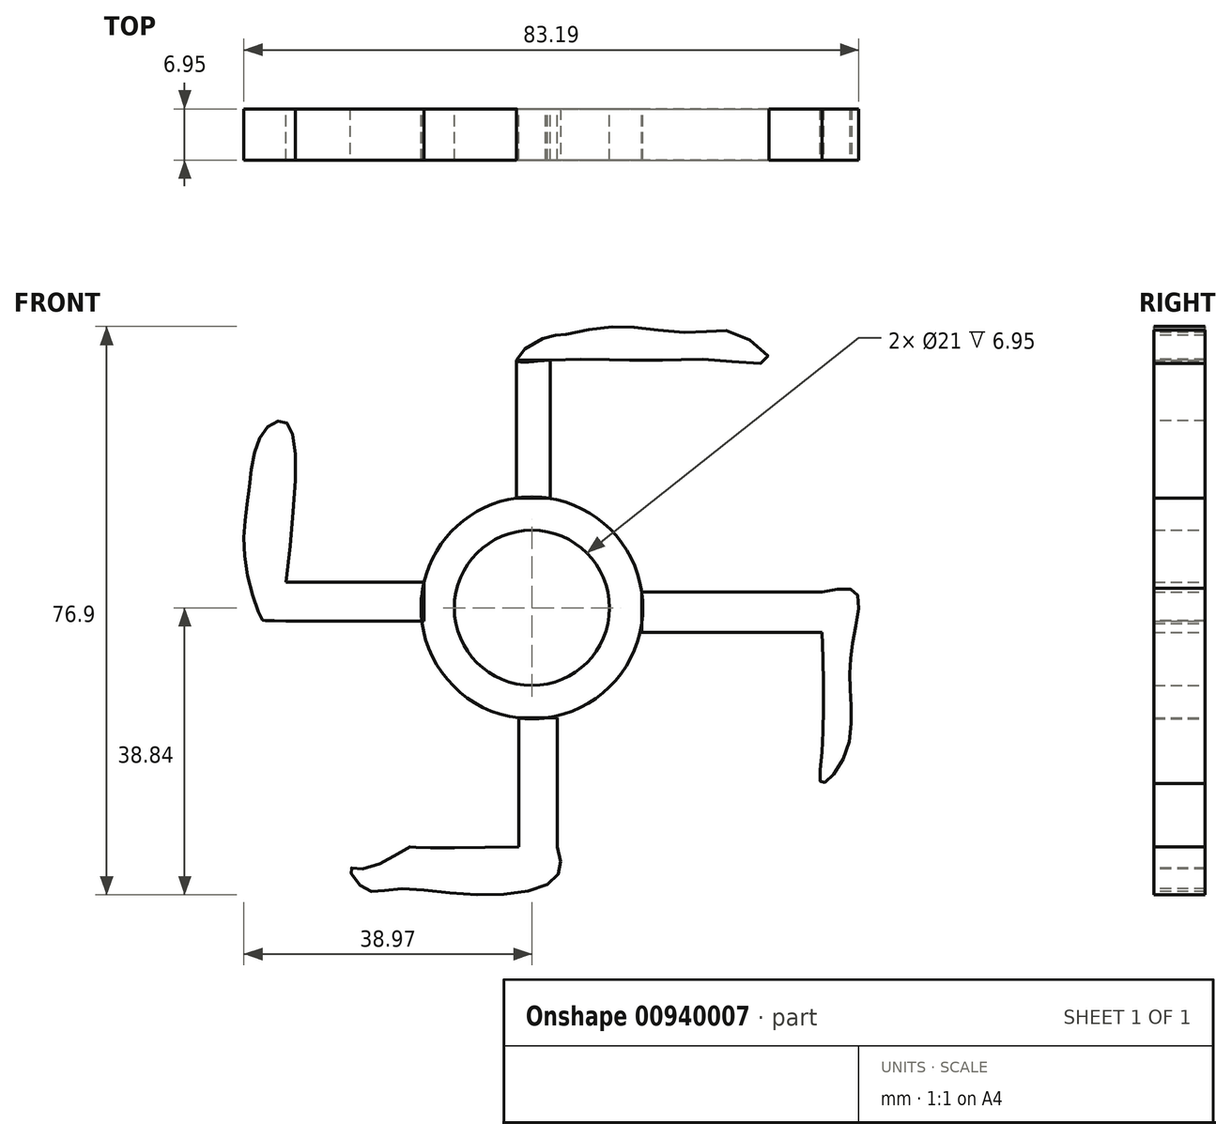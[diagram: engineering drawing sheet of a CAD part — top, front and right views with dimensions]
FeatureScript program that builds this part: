
annotation { "Feature Type Name" : "Feature", "Feature Type Description" : "" }
export const myFeature = defineFeature(function(context is Context, id is Id, definition is map)
    precondition{}
    {
        {
            var Q0;
            Q0=qCreatedBy(makeId("Front.planeOp"),FACE);
            var sketch = newSketch(context, id + "F0", { "sketchPlane" : qUnion([Q0])});
            skCircle(sketch, "E0", {"center": v(0, 0) * mm, "radius": 15 * mm});
            skCircle(sketch, "E1", {"center": v(0, 0) * mm, "radius": 10.5 * mm});
            skLineSegment(sketch, "E2.bottom", {"start": v(-2.08, 14.86) * mm, "end": v(2.45, 14.86) * mm});
            skLineSegment(sketch, "E2.top", {"start": v(-2.08, 33.54) * mm, "end": v(2.45, 33.54) * mm});
            skLineSegment(sketch, "E2.left", {"start": v(-2.08, 14.86) * mm, "end": v(-2.08, 33.54) * mm});
            skLineSegment(sketch, "E2.right", {"start": v(2.45, 14.86) * mm, "end": v(2.45, 33.54) * mm});
            skFitSpline(sketch, "E3", {"points": [v(-2.08, 33.54) * mm, v(0, 35.7) * mm, v(3.04, 36.87) * mm, v(3.63, 36.87) * mm, v(8.92, 37.85) * mm, v(14.8, 37.85) * mm, v(22.46, 37.27) * mm, v(27.36, 37.27) * mm, v(32.07, 33.54) * mm, v(24.81, 33.54) * mm, v(18.93, 33.54) * mm, v(15, 33.54) * mm, v(12.06, 33.54) * mm, v(2.45, 33.54) * mm, v(-2.08, 33.54) * mm]});
            skLineSegment(sketch, "E4.bottom", {"start": v(14.85, 2.11) * mm, "end": v(39.23, 2.11) * mm});
            skLineSegment(sketch, "E4.top", {"start": v(14.85, -3.33) * mm, "end": v(39.23, -3.33) * mm});
            skLineSegment(sketch, "E4.left", {"start": v(14.85, 2.11) * mm, "end": v(14.85, -3.33) * mm});
            skLineSegment(sketch, "E4.right", {"start": v(39.23, 2.11) * mm, "end": v(39.23, -3.33) * mm});
            skLineSegment(sketch, "E5.bottom", {"start": v(-1.8, -14.9) * mm, "end": v(3.43, -14.9) * mm});
            skLineSegment(sketch, "E5.top", {"start": v(-1.8, -32.36) * mm, "end": v(3.43, -32.36) * mm});
            skLineSegment(sketch, "E5.left", {"start": v(-1.8, -14.9) * mm, "end": v(-1.8, -32.36) * mm});
            skLineSegment(sketch, "E5.right", {"start": v(3.43, -14.9) * mm, "end": v(3.43, -32.36) * mm});
            skLineSegment(sketch, "E6.bottom", {"start": v(-14.6, 3.46) * mm, "end": v(-33.25, 3.46) * mm});
            skLineSegment(sketch, "E6.top", {"start": v(-14.6, -1.77) * mm, "end": v(-33.25, -1.77) * mm});
            skLineSegment(sketch, "E6.left", {"start": v(-14.6, 3.46) * mm, "end": v(-14.6, -1.77) * mm});
            skLineSegment(sketch, "E6.right", {"start": v(-33.25, 3.46) * mm, "end": v(-33.25, -1.77) * mm});
            skFitSpline(sketch, "E7", {"points": [v(3.43, -32.36) * mm, v(3.43, -36.29) * mm, v(-5.59, -38.84) * mm, v(-18.73, -38.05) * mm, v(-22.65, -38.05) * mm, v(-24.62, -35.3) * mm, v(-22.65, -35.3) * mm, v(-16.57, -32.36) * mm, v(-15.79, -32.36) * mm, v(-1.8, -32.36) * mm], "startDerivative": vector(12.64, -46.06) * mm, "endDerivative": vector(106.45, 1.35) * mm});
            skFitSpline(sketch, "E8", {"points": [v(-33.25, -1.77) * mm, v(-36.19, -1.77) * mm, v(-36.38, -1.77) * mm, v(-38.74, 5.88) * mm, v(-38.35, 15.5) * mm, v(-36.38, 23.73) * mm, v(-33.25, 25.1) * mm, v(-33.25, 3.46) * mm], "startDerivative": vector(-39.27, 1.4) * mm, "endDerivative": vector(-12.27, -113.4) * mm});
            skFitSpline(sketch, "E9", {"points": [v(39.23, 2.11) * mm, v(43.84, 2.11) * mm, v(43.44, -4.32) * mm, v(43.05, -10.98) * mm, v(42.46, -19.61) * mm, v(39.23, -23.73) * mm, v(39.23, -19.42) * mm, v(39.23, -3.33) * mm], "startDerivative": vector(50.34, 11.69) * mm, "endDerivative": vector(-2.74, 81.14) * mm});
            skSolve(sketch);
        }
        {
            var Q0;
            Q0=makeQuery(id+"F0.imprint","IMPRINT",FACE,{"disambiguationData":[TD([[makeQuery(id+"F0.imprint","IMPRINT",EDGE,{"derivedFrom":sQuery(id+"F0.wireOp",EDGE,"E6.right")}),-1.0]])]});
            var Q1;
            {var subQ0=sQuery(id+"F0.wireOp",EDGE,"E6.bottom");Q1=makeQuery(id+"F0.imprint","IMPRINT",FACE,{"disambiguationData":[TD([[makeQuery(id+"F0.imprint","IMPRINT",EDGE,{"derivedFrom":subQ0}),1.0]])]});}
            var Q2;
            Q2=makeQuery(id+"F0.imprint","IMPRINT",FACE,{"disambiguationData":[TD([[makeQuery(id+"F0.imprint","IMPRINT",EDGE,{"derivedFrom":sQuery(id+"F0.wireOp",EDGE,"E1")}),-1.0]])]});
            var Q3;
            {var subQ1=sQuery(id+"F0.wireOp",EDGE,"E2.left");Q3=makeQuery(id+"F0.imprint","IMPRINT",FACE,{"disambiguationData":[TD([[makeQuery(id+"F0.imprint","IMPRINT",EDGE,{"derivedFrom":subQ1}),-1.0]])]});}
            var Q4;
            {var subQ0=sQuery(id+"F0.wireOp",EDGE,"E2.top");Q4=makeQuery(id+"F0.imprint","IMPRINT",FACE,{"disambiguationData":[TD([[makeQuery(id+"F0.imprint","IMPRINT",EDGE,{"derivedFrom":subQ0}),1.0]])]});}
            var Q5;
            Q5=makeQuery(id+"F0.imprint","IMPRINT",FACE,{"disambiguationData":[TD([[makeQuery(id+"F0.imprint","IMPRINT",EDGE,{"derivedFrom":sQuery(id+"F0.wireOp",EDGE,"E4.right")}),1.0]])]});
            var Q6;
            {var subQ4=sQuery(id+"F0.wireOp",EDGE,"E4.bottom");Q6=makeQuery(id+"F0.imprint","IMPRINT",FACE,{"disambiguationData":[TD([[makeQuery(id+"F0.imprint","IMPRINT",EDGE,{"derivedFrom":subQ4}),-1.0]])]});}
            var Q7;
            Q7=makeQuery(id+"F0.imprint","IMPRINT",FACE,{"disambiguationData":[TD([[makeQuery(id+"F0.imprint","IMPRINT",EDGE,{"derivedFrom":sQuery(id+"F0.wireOp",EDGE,"E5.top")}),1.0]])]});
            var Q8;
            Q8=makeQuery(id+"F0.imprint","IMPRINT",FACE,{"disambiguationData":[TD([[makeQuery(id+"F0.imprint","IMPRINT",EDGE,{"derivedFrom":sQuery(id+"F0.wireOp",EDGE,"E5.top")}),-1.0]])]});
            extrude(context, id + "F1", {"entities" : qUnion([Q0, Q1, Q2, Q3, Q4, Q5, Q6, Q7, Q8]), "depth" : 6.95 * mm, "offsetDistance" : 25 * mm});
        }
    });
